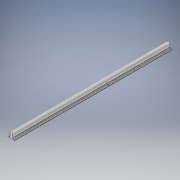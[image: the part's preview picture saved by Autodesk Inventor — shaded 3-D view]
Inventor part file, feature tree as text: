
AUTODESK INVENTOR PART (.ipt)
format: ipt  version: 2019 (Build 230136000, 136)  size: 207,360 bytes
history: native  units: in
note: dims shown in document units (in); Inventor stores cm internally (conversion verified against a paired STEP export)
features: extrude x1, sketch x1, projected_geometry x1, other x1, chamfer x1
ambient origin geometry x8: Origin, YZ Plane, XZ Plane, XY Plane, X Axis, Y Axis, Z Axis, Center Point
bodies: Solid1 (feature_tree), Solid2 (feature_tree)
feature tree (5):
  extrude  "Extrusion1"  [1 undecoded]
  sketch  "Sketch1"  dims[d0=23.622in d1=0.0in]
  projected_geometry  "Projected Loop1"
  other  "Boss-Extrude1"
  chamfer  "Chamfer1"  [1 undecoded]
note: 2 required parameter values undecoded (feature->parameter linkage not recoverable at this tier; creation-order binding heuristic only, values carry confidence <= 0.55)
